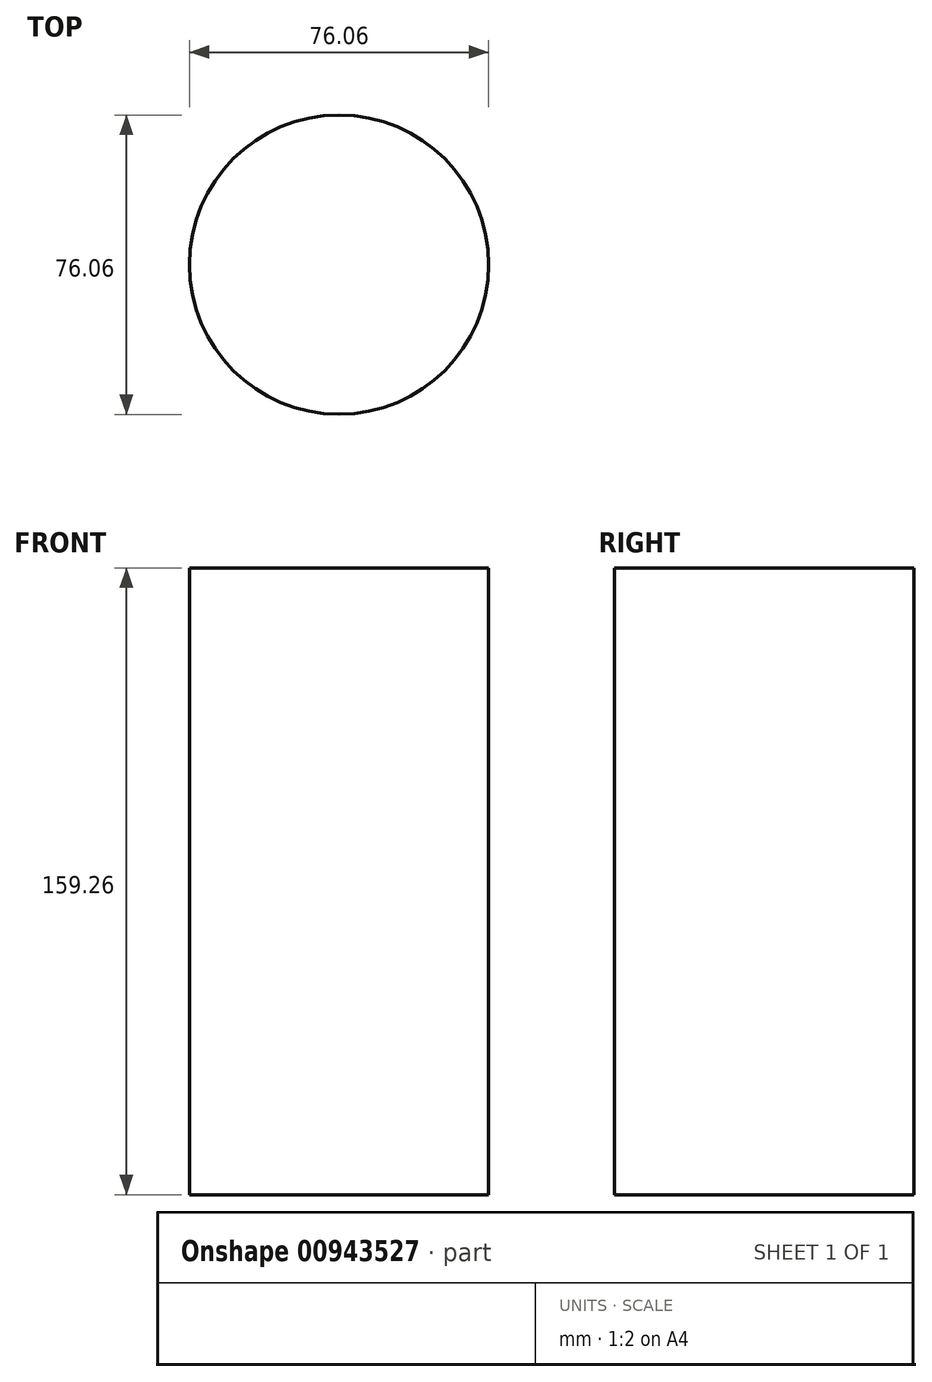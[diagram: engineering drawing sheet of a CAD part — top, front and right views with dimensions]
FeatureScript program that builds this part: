
annotation { "Feature Type Name" : "Feature", "Feature Type Description" : "" }
export const myFeature = defineFeature(function(context is Context, id is Id, definition is map)
    precondition{}
    {
        {
            var Q0;
            Q0=qCreatedBy(makeId("Top.planeOp"),FACE);
            var sketch = newSketch(context, id + "F0", { "sketchPlane" : qUnion([Q0])});
            skCircle(sketch, "E0", {"center": v(0, 0) * mm, "radius": 38.03 * mm});
            skSolve(sketch);
        }
        {
            var Q0;
            Q0=makeQuery(id+"F0.imprint","IMPRINT",FACE,{"disambiguationData":[TD([[makeQuery(id+"F0.imprint","IMPRINT",EDGE,{"derivedFrom":sQuery(id+"F0.wireOp",EDGE,"E0")}),1.0]])]});
            extrude(context, id + "F1", {"entities" : qUnion([Q0]), "oppositeDirection" : true, "depth" : 159.26 * mm, "offsetDistance" : 25.4 * mm});
        }
    });
